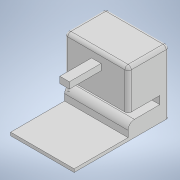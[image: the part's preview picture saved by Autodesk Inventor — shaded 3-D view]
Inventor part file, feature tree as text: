
AUTODESK INVENTOR PART (.ipt)
format: ipt  version: 2022 (Build 260153000, 153)  size: 161,280 bytes
history: native  units: in
note: dims shown in document units (in); Inventor stores cm internally (conversion verified against a paired STEP export)
features: extrude x4, sketch x4, fillet x1
ambient origin geometry x8: Origin, YZ Plane, XZ Plane, XY Plane, X Axis, Y Axis, Z Axis, Center Point
bodies: Solid1 (feature_tree)
feature tree (9):
  extrude  "Extrusion1"  Depth=15.0in
  extrude  "Extrusion2"  Depth=8.5in
  extrude  "Extrusion3"  Depth=0.5in
  extrude  "Extrusion4"  Depth=4.0in
  fillet  "Fillet1"  Radius=1.25in
  sketch  "Sketch1"  dims[d0=10.0in d1=15.0in]
  sketch  "Sketch2"  dims[d2=10.0in d3=0.0in d4=8.5in]
  sketch  "Sketch3"  dims[d6=1.0in d7=0.5in]
  sketch  "Sketch4"  dims[d8=1.0in d9=4.0in d10=1.25in d11=1.0in d12=7.0in d13=1.0in d14=5.0in d15=0.0in d16=0.0in d17=1.5in d18=1.0in d19=0.0in d20=0.25in d21=4.375in d22=0.75in d23=1.0in d24=0.0in d25=0.5in]
